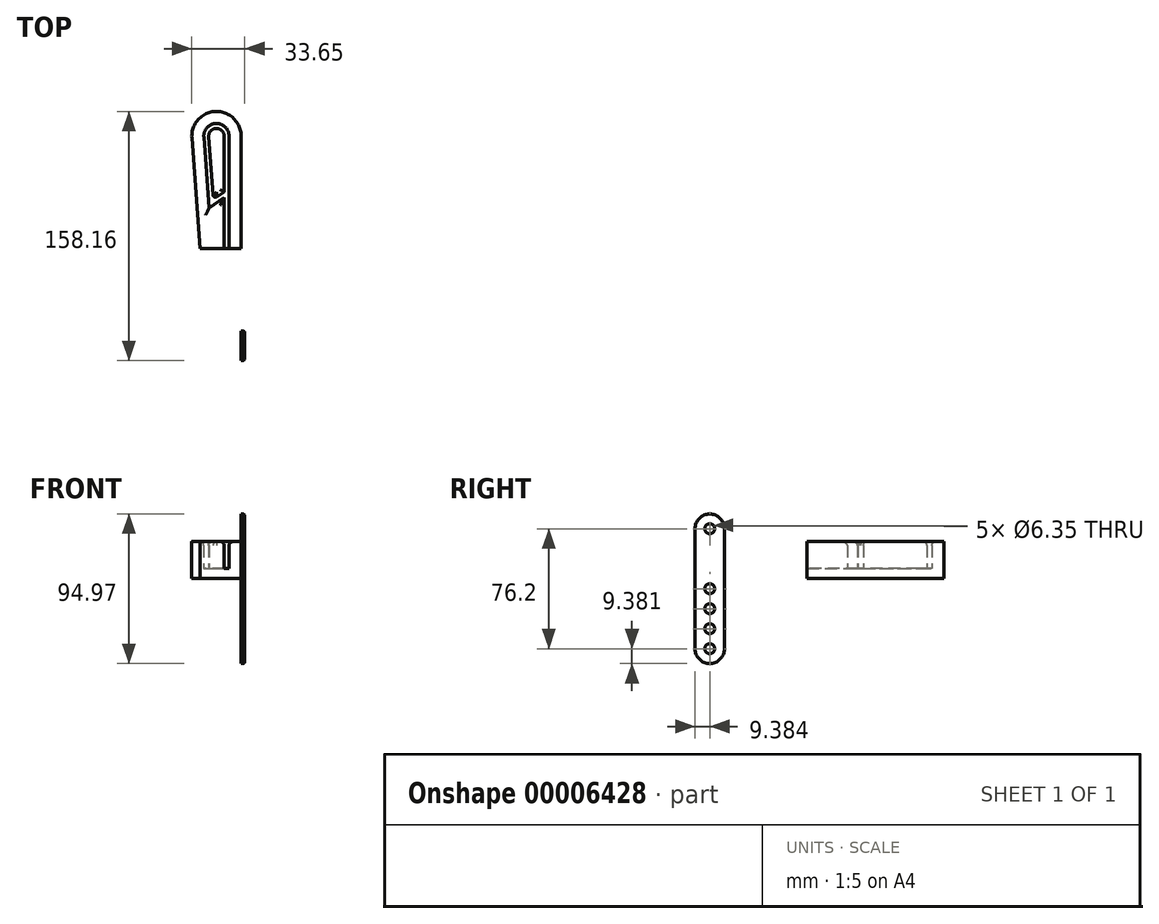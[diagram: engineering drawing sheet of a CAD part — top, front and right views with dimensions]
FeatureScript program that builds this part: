
annotation { "Feature Type Name" : "Feature", "Feature Type Description" : "" }
export const myFeature = defineFeature(function(context is Context, id is Id, definition is map)
    precondition{}
    {
        {
            var Q0;
            Q0=qCreatedBy(makeId("Right.planeOp"),FACE);
            var sketch = newSketch(context, id + "F0", { "sketchPlane" : qUnion([Q0])});
            skLineSegment(sketch, "E0.left", {"start": v(-71.22, 25.06) * mm, "end": v(-71.22, -51.14) * mm});
            skLineSegment(sketch, "E0.right", {"start": v(-52.45, 25.06) * mm, "end": v(-52.45, -51.14) * mm});
            skArc(sketch, "E1", {"start": v(-71.22, -51.14) * mm, "mid": v(-61.84, -60.52) * mm, "end": v(-52.45, -51.14) * mm});
            skArc(sketch, "E2", {"start": v(-52.45, 25.06) * mm, "mid": v(-61.84, 34.45) * mm, "end": v(-71.22, 25.06) * mm});
            skCircle(sketch, "E3", {"center": v(-61.84, 25.06) * mm, "radius": 3.18 * mm});
            skCircle(sketch, "E4", {"center": v(-61.84, -13.04) * mm, "radius": 3.17 * mm});
            skCircle(sketch, "E5", {"center": v(-61.84, -25.74) * mm, "radius": 3.17 * mm});
            skCircle(sketch, "E6", {"center": v(-61.84, -38.44) * mm, "radius": 3.17 * mm});
            skCircle(sketch, "E7", {"center": v(-61.84, -51.14) * mm, "radius": 3.17 * mm});
            skLineSegment(sketch, "E8", {"start": v(-65.01, 29.36) * mm, "end": v(-65.01, -53.42) * mm, "construction": true});
            skLineSegment(sketch, "E9", {"start": v(-61.84, 34.45) * mm, "end": v(-105.3, 34.45) * mm, "construction": true});
            skSolve(sketch);
        }
        {
            var Q0;
            Q0 = qSketchRegion(id + "F0", true);
            extrude(context, id + "F1", {"entities" : qUnion([Q0]), "depth" : 2.36 * mm});
        }
        {
            var Q0;
            Q0=makeQuery(id+"F1.opExtrude","CAP_EDGE",EDGE,{"disambiguationData":[OSD([sQuery(id+"F0.wireOp",EDGE,"E0.left")])],"isStart":false});
            var Q1;
            Q1=makeQuery(id+"F1.opExtrude","CAP_EDGE",EDGE,{"disambiguationData":[OSD([sQuery(id+"F0.wireOp",EDGE,"E2")])],"isStart":false});
            var Q2;
            Q2=makeQuery(id+"F1.opExtrude","CAP_EDGE",EDGE,{"disambiguationData":[OSD([sQuery(id+"F0.wireOp",EDGE,"E0.right")])],"isStart":false});
            var Q3;
            Q3=makeQuery(id+"F1.opExtrude","CAP_EDGE",EDGE,{"disambiguationData":[OSD([sQuery(id+"F0.wireOp",EDGE,"E1")])],"isStart":false});
            fillet(context, id + "F2", {"entities" : qUnion([Q0, Q1, Q2, Q3]), "radius" : 1.27 * mm, "tangentPropagation" : true, "allowEdgeOverflow" : false});
        }
        {
            var Q0;
            Q0=qCreatedBy(makeId("Top.planeOp"),FACE);
            var sketch = newSketch(context, id + "F3", { "sketchPlane" : qUnion([Q0])});
            skLineSegment(sketch, "E10", {"start": v(-10.74, 35.9) * mm, "end": v(-10.74, 71.3) * mm});
            skLineSegment(sketch, "E11", {"start": v(-20.54, 70.94) * mm, "end": v(-17.84, 33.84) * mm});
            skLineSegment(sketch, "E12", {"start": v(-15.47, 32.7) * mm, "end": v(-10.74, 35.9) * mm});
            skArc(sketch, "E13", {"start": v(-10.74, 71.3) * mm, "mid": v(-15.82, 76.2) * mm, "end": v(-20.54, 70.94) * mm});
            skLineSegment(sketch, "E14.0", {"start": v(-20.38, 25.59) * mm, "end": v(-10.74, 32.12) * mm});
            skLineSegment(sketch, "E14.1", {"start": v(-23.65, 70.72) * mm, "end": v(-20.38, 25.59) * mm});
            skArc(sketch, "E14.2", {"start": v(-7.62, 71.3) * mm, "mid": v(-15.94, 79.32) * mm, "end": v(-23.65, 70.72) * mm});
            skLineSegment(sketch, "E14.3", {"start": v(-7.62, 0) * mm, "end": v(-7.62, 71.3) * mm});
            skLineSegment(sketch, "E15", {"start": v(-10.74, 32.12) * mm, "end": v(-10.74, 0) * mm});
            skLineSegment(sketch, "E16", {"start": v(0, 0) * mm, "end": v(0, 71.3) * mm});
            skLineSegment(sketch, "E17", {"start": v(-31.25, 70.17) * mm, "end": v(-26.16, 0) * mm});
            skArc(sketch, "E18", {"start": v(0, 71.3) * mm, "mid": v(-16.21, 86.93) * mm, "end": v(-31.25, 70.17) * mm});
            skLineSegment(sketch, "E19", {"start": v(-10.74, 0) * mm, "end": v(-7.62, 0) * mm});
            skLineSegment(sketch, "E20", {"start": v(-26.16, 0) * mm, "end": v(0, 0) * mm});
            skPoint(sketch, "E21.visualSharp", {"position": v(-17.65, 31.21) * mm});
            skArc(sketch, "E21.filletArc", {"start": v(-17.84, 33.84) * mm, "mid": v(-16.99, 32.58) * mm, "end": v(-15.47, 32.7) * mm});
            skLineSegment(sketch, "E22", {"start": v(-8.38, 2.22) * mm, "end": v(-8.38, 0) * mm, "construction": true});
            skSolve(sketch);
        }
        {
            var Q0;
            Q0=makeQuery(id+"F3.imprint","IMPRINT",FACE,{"disambiguationData":[TD([[makeQuery(id+"F3.imprint","IMPRINT",EDGE,{"derivedFrom":sQuery(id+"F3.wireOp",EDGE,"E14.0")}),-1.0]])]});
            var Q1;
            Q1=makeQuery(id+"F3.imprint","IMPRINT",FACE,{"disambiguationData":[TD([[makeQuery(id+"F3.imprint","IMPRINT",EDGE,{"derivedFrom":sQuery(id+"F3.wireOp",EDGE,"E10")}),1.0]])]});
            var Q2;
            Q2=makeQuery(id+"F3.imprint","IMPRINT",FACE,{"disambiguationData":[TD([[makeQuery(id+"F3.imprint","IMPRINT",EDGE,{"derivedFrom":sQuery(id+"F3.wireOp",EDGE,"E10")}),-1.0]])]});
            extrude(context, id + "F4", {"entities" : qUnion([Q0, Q1, Q2]), "oppositeDirection" : true, "depth" : 6.35 * mm});
        }
        {
            var Q0;
            Q0=makeQuery(id+"F3.imprint","IMPRINT",FACE,{"disambiguationData":[TD([[makeQuery(id+"F3.imprint","IMPRINT",EDGE,{"derivedFrom":sQuery(id+"F3.wireOp",EDGE,"E10")}),1.0]])]});
            var Q1;
            Q1=makeQuery(id+"F3.imprint","IMPRINT",FACE,{"disambiguationData":[TD([[makeQuery(id+"F3.imprint","IMPRINT",EDGE,{"derivedFrom":sQuery(id+"F3.wireOp",EDGE,"E14.0")}),-1.0]])]});
            extrude(context, id + "F5", {"entities" : qUnion([Q0, Q1]), "operationType" : NewBodyOperationType.ADD, "depth" : 16.94 * mm});
        }
        {
            var Q0;
            Q0=makeQuery(id+"F5.opExtrude","CAP_EDGE",EDGE,{"disambiguationData":[OSD([sQuery(id+"F3.wireOp",EDGE,"E14.3")])],"isStart":false});
            var Q1;
            Q1=makeQuery(id+"F5.opExtrude","CAP_EDGE",EDGE,{"disambiguationData":[OSD([sQuery(id+"F3.wireOp",EDGE,"E10")])],"isStart":false});
            var Q2;
            Q2=makeQuery(id+"F5.opExtrude","CAP_EDGE",EDGE,{"disambiguationData":[OSD([sQuery(id+"F3.wireOp",EDGE,"E12")])],"isStart":false});
            var Q3;
            Q3=makeQuery(id+"F5.opExtrude","CAP_EDGE",EDGE,{"disambiguationData":[OSD([sQuery(id+"F3.wireOp",EDGE,"E21.filletArc")])],"isStart":false});
            var Q4;
            Q4=makeQuery(id+"F5.opExtrude","CAP_EDGE",EDGE,{"disambiguationData":[OSD([sQuery(id+"F3.wireOp",EDGE,"E11")])],"isStart":false});
            var Q5;
            Q5=makeQuery(id+"F5.opExtrude","CAP_EDGE",EDGE,{"disambiguationData":[OSD([sQuery(id+"F3.wireOp",EDGE,"E14.1")])],"isStart":false});
            var Q6;
            Q6=makeQuery(id+"F5.opExtrude","CAP_EDGE",EDGE,{"disambiguationData":[OSD([sQuery(id+"F3.wireOp",EDGE,"E14.0")])],"isStart":false});
            var Q7;
            Q7=makeQuery(id+"F5.opExtrude","CAP_EDGE",EDGE,{"disambiguationData":[OSD([sQuery(id+"F3.wireOp",EDGE,"E15")])],"isStart":false});
            var Q8;
            Q8=makeQuery(id+"F5.opExtrude","CAP_EDGE",EDGE,{"disambiguationData":[OSD([sQuery(id+"F3.wireOp",EDGE,"E14.2")])],"isStart":false});
            var Q9;
            Q9=makeQuery(id+"F5.opExtrude","CAP_EDGE",EDGE,{"disambiguationData":[OSD([sQuery(id+"F3.wireOp",EDGE,"E13")])],"isStart":false});
            fillet(context, id + "F6", {"entities" : qUnion([Q0, Q1, Q2, Q3, Q4, Q5, Q6, Q7, Q8, Q9]), "radius" : 2.54 * mm, "allowEdgeOverflow" : false});
        }
    });
